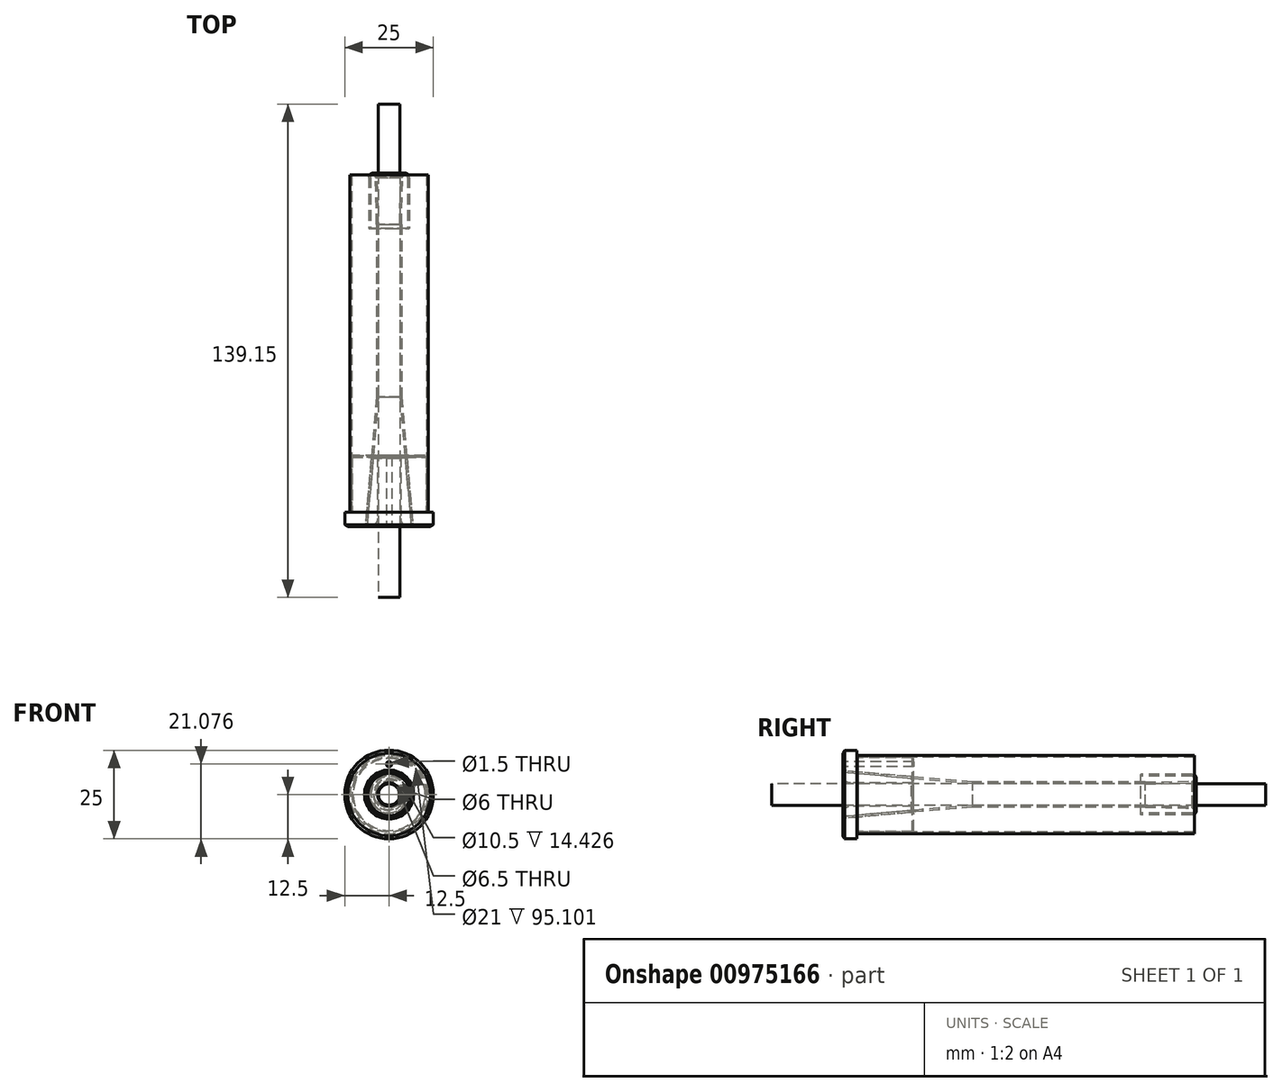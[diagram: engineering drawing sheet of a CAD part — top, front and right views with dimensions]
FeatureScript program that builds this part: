
annotation { "Feature Type Name" : "Feature", "Feature Type Description" : "" }
export const myFeature = defineFeature(function(context is Context, id is Id, definition is map)
    precondition{}
    {
        {
            var Q0;
            Q0=qCreatedBy(makeId("Right.planeOp"),FACE);
            var sketch = newSketch(context, id + "F0", { "sketchPlane" : qUnion([Q0])});
            skLineSegment(sketch, "E0.bottom", {"start": v(-20, 0) * mm, "end": v(119.15, 0) * mm});
            skLineSegment(sketch, "E0.top", {"start": v(-20, 3) * mm, "end": v(119.15, 3) * mm});
            skLineSegment(sketch, "E0.left", {"start": v(-20, 0) * mm, "end": v(-20, 3) * mm});
            skLineSegment(sketch, "E0.right", {"start": v(119.15, 0) * mm, "end": v(119.15, 3) * mm});
            skLineSegment(sketch, "E1", {"start": v(0, 3.25) * mm, "end": v(20, 3.25) * mm});
            skLineSegment(sketch, "E2", {"start": v(0, 3.25) * mm, "end": v(0, 6.2) * mm});
            skLineSegment(sketch, "E3", {"start": v(0, 6.2) * mm, "end": v(20, 4.45) * mm});
            skLineSegment(sketch, "E4", {"start": v(20, 4.45) * mm, "end": v(20, 3.25) * mm});
            skLineSegment(sketch, "E5", {"start": v(0, 6.75) * mm, "end": v(20, 5) * mm});
            skLineSegment(sketch, "E6", {"start": v(0, 6.75) * mm, "end": v(0, 7.83) * mm});
            skLineSegment(sketch, "E7", {"start": v(0, 12.5) * mm, "end": v(4, 12.5) * mm});
            skLineSegment(sketch, "E8", {"start": v(4, 12.5) * mm, "end": v(4, 10.4) * mm});
            skLineSegment(sketch, "E9", {"start": v(4, 10.4) * mm, "end": v(20, 10.4) * mm});
            skLineSegment(sketch, "E10", {"start": v(20, 10.4) * mm, "end": v(20, 9.33) * mm});
            skLineSegment(sketch, "E11", {"start": v(0, 9.33) * mm, "end": v(20, 9.33) * mm, "construction": true});
            skLineSegment(sketch, "E12", {"start": v(20, 8.58) * mm, "end": v(0, 8.58) * mm, "construction": true});
            skLineSegment(sketch, "E13", {"start": v(0, 7.83) * mm, "end": v(20, 7.83) * mm, "construction": true});
            skArc(sketch, "E14", {"start": v(0, 5.5) * mm, "mid": v(0.66, 3.9) * mm, "end": v(2.25, 3.25) * mm});
            skLineSegment(sketch, "E15", {"start": v(0, 5.97) * mm, "end": v(0.21, 6.18) * mm});
            skLineSegment(sketch, "E16", {"start": v(20, 4.26) * mm, "end": v(19.79, 4.47) * mm});
            skLineSegment(sketch, "E17", {"start": v(20, 3.46) * mm, "end": v(19.79, 3.25) * mm});
            skLineSegment(sketch, "E18", {"start": v(0, 11.63) * mm, "end": v(0.5, 12.5) * mm});
            skLineSegment(sketch, "E19", {"start": v(0, 6.95) * mm, "end": v(0.21, 6.73) * mm});
            skLineSegment(sketch, "E20", {"start": v(19.57, 10.4) * mm, "end": v(20, 10.15) * mm});
            skLineSegment(sketch, "E21", {"start": v(20, 5.43) * mm, "end": v(19.35, 5.06) * mm});
            skLineSegment(sketch, "E22", {"start": v(20, 9.33) * mm, "end": v(20, 5) * mm});
            skLineSegment(sketch, "E23", {"start": v(0, 7.83) * mm, "end": v(0, 12.5) * mm});
            skLineSegment(sketch, "E24", {"start": v(80, 10.4) * mm, "end": v(80, 3.8) * mm});
            skLineSegment(sketch, "E25", {"start": v(80, 3.8) * mm, "end": v(98.43, 3.8) * mm});
            skLineSegment(sketch, "E26", {"start": v(80, 10.4) * mm, "end": v(84, 10.4) * mm});
            skLineSegment(sketch, "E27", {"start": v(84, 10.4) * mm, "end": v(84, 5.25) * mm});
            skLineSegment(sketch, "E28", {"start": v(84, 5.25) * mm, "end": v(98.43, 5.25) * mm});
            skLineSegment(sketch, "E29", {"start": v(80, 9.33) * mm, "end": v(84, 9.33) * mm, "construction": true});
            skLineSegment(sketch, "E30", {"start": v(80, 8.58) * mm, "end": v(84, 8.58) * mm, "construction": true});
            skLineSegment(sketch, "E31", {"start": v(80, 7.83) * mm, "end": v(84, 7.83) * mm, "construction": true});
            skLineSegment(sketch, "E32", {"start": v(98.43, 5.25) * mm, "end": v(98.43, 3.8) * mm, "construction": true});
            skArc(sketch, "E33", {"start": v(98.43, 5.25) * mm, "mid": v(99.15, 4.53) * mm, "end": v(98.43, 3.8) * mm});
            skArc(sketch, "E34", {"start": v(84, 7.68) * mm, "mid": v(84.71, 5.96) * mm, "end": v(86.43, 5.25) * mm});
            skLineSegment(sketch, "E35", {"start": v(80.43, 10.4) * mm, "end": v(80, 10.15) * mm});
            skArc(sketch, "E36", {"start": v(80, 6.05) * mm, "mid": v(80.66, 4.46) * mm, "end": v(82.25, 3.8) * mm});
            skLineSegment(sketch, "E37", {"start": v(82, 10.4) * mm, "end": v(82, 9.33) * mm, "construction": true});
            skLineSegment(sketch, "E38.MirrorCS", {"start": v(83.57, 10.4) * mm, "end": v(84, 10.15) * mm});
            skLineSegment(sketch, "E39.bottom", {"start": v(4.05, 11) * mm, "end": v(99.15, 11) * mm});
            skLineSegment(sketch, "E39.top", {"start": v(4.05, 10.5) * mm, "end": v(99.15, 10.5) * mm});
            skLineSegment(sketch, "E39.left", {"start": v(4.05, 11) * mm, "end": v(4.05, 10.5) * mm});
            skLineSegment(sketch, "E39.right", {"start": v(99.15, 11) * mm, "end": v(99.15, 10.5) * mm});
            skPoint(sketch, "E40", {"position": v(99.15, 4.53) * mm});
            skSolve(sketch);
        }
        {
            var Q0;
            Q0=qCreatedBy(makeId("Front.planeOp"),FACE);
            var sketch = newSketch(context, id + "F1", { "sketchPlane" : qUnion([Q0])});
            skPoint(sketch, "E41.0", {"position": v(0, 8.58) * mm});
            skPoint(sketch, "E42.0", {"position": v(0, 9.33) * mm});
            skCircle(sketch, "E43", {"center": v(0, 8.58) * mm, "radius": 0.75 * mm});
            skLineSegment(sketch, "E44", {"start": v(0, 0) * mm, "end": v(2.21, 0) * mm, "construction": true});
            skCircle(sketch, "E45.MirrorC", {"center": v(0, -8.58) * mm, "radius": 0.75 * mm});
            skSolve(sketch);
        }
        {
            var Q0;
            Q0=qCreatedBy(makeId("Right.planeOp"),FACE);
            var sketch = newSketch(context, id + "F2", { "sketchPlane" : qUnion([Q0])});
            skLineSegment(sketch, "E46.0", {"start": v(-20, 0) * mm, "end": v(119.15, 0) * mm, "construction": true});
            skLineSegment(sketch, "E47.0", {"start": v(-20, 3) * mm, "end": v(119.15, 3) * mm});
            skLineSegment(sketch, "E48.0", {"start": v(0, 6.2) * mm, "end": v(20, 4.45) * mm});
            skLineSegment(sketch, "E49.0", {"start": v(84, 5.25) * mm, "end": v(98.43, 5.25) * mm});
            skArc(sketch, "E50.0", {"start": v(98.43, 5.25) * mm, "mid": v(99.15, 4.53) * mm, "end": v(98.43, 3.8) * mm});
            skLineSegment(sketch, "E51.0", {"start": v(80, 3.8) * mm, "end": v(98.43, 3.8) * mm, "construction": true});
            skLineSegment(sketch, "E52", {"start": v(20, 4.45) * mm, "end": v(36.57, 3) * mm});
            skLineSegment(sketch, "E53.0", {"start": v(20.03, 4.95) * mm, "end": v(36.57, 3.5) * mm});
            skLineSegment(sketch, "E53.1", {"start": v(0, 6.7) * mm, "end": v(20.03, 4.95) * mm});
            skLineSegment(sketch, "E54", {"start": v(0, 6.7) * mm, "end": v(0, 6.2) * mm});
            skLineSegment(sketch, "E55", {"start": v(36.57, 3.5) * mm, "end": v(85.22, 3.5) * mm});
            skArc(sketch, "E56.0", {"start": v(98.43, 5.75) * mm, "mid": v(99.65, 4.53) * mm, "end": v(98.43, 3.3) * mm});
            skLineSegment(sketch, "E56.1", {"start": v(84, 5.75) * mm, "end": v(98.43, 5.75) * mm});
            skLineSegment(sketch, "E57", {"start": v(84, 5.75) * mm, "end": v(84, 5.25) * mm});
            skLineSegment(sketch, "E58", {"start": v(85.22, 3.5) * mm, "end": v(98.43, 3.8) * mm});
            skLineSegment(sketch, "E59", {"start": v(98.43, 3.3) * mm, "end": v(85.22, 3) * mm});
            skSolve(sketch);
        }
        {
            var Q0;
            Q0=makeQuery(id+"F0.imprint","IMPRINT",FACE,{"disambiguationData":[TD([[makeQuery(id+"F0.imprint","IMPRINT",EDGE,{"derivedFrom":sQuery(id+"F0.wireOp",EDGE,"E0.bottom")}),1.0]])]});
            var Q1;
            {var subQ7=sQuery(id+"F0.wireOp",EDGE,"E8");Q1=makeQuery(id+"F0.imprint","IMPRINT",FACE,{"disambiguationData":[TD([[makeQuery(id+"F0.imprint","IMPRINT",EDGE,{"derivedFrom":subQ7}),-1.0]])]});}
            var Q2;
            {var subQ5=sQuery(id+"F0.wireOp",EDGE,"E14");Q2=makeQuery(id+"F0.imprint","IMPRINT",FACE,{"disambiguationData":[TD([[makeQuery(id+"F0.imprint","IMPRINT",EDGE,{"derivedFrom":subQ5}),1.0]])]});}
            var Q3;
            {var subQ1=sQuery(id+"F0.wireOp",EDGE,"E33");Q3=makeQuery(id+"F0.imprint","IMPRINT",FACE,{"disambiguationData":[TD([[makeQuery(id+"F0.imprint","IMPRINT",EDGE,{"derivedFrom":subQ1}),-1.0]])]});}
            var Q4;
            Q4=makeQuery(id+"F0.imprint","IMPRINT",FACE,{"disambiguationData":[TD([[makeQuery(id+"F0.imprint","IMPRINT",EDGE,{"derivedFrom":sQuery(id+"F0.wireOp",EDGE,"E39.bottom")}),-1.0]])]});
            var Q5;
            Q5=sQuery(id+"F0.wireOp",EDGE,"E0.bottom");
            revolve(context, id + "F3", {"surfaceOperationType" : NewSurfaceOperationType.NEW, "entities" : qUnion([Q0, Q1, Q2, Q3, Q4]), "axis" : qUnion([Q5]), "revolveType" : RevolveType.FULL});
        }
        {
            var Q0;
            Q0=makeQuery(id+"F1.imprint","IMPRINT",FACE,{"disambiguationData":[TD([[makeQuery(id+"F1.imprint","IMPRINT",EDGE,{"derivedFrom":sQuery(id+"F1.wireOp",EDGE,"E45.MirrorC")}),-1.0]])]});
            var Q1;
            Q1=makeQuery(id+"F1.imprint","IMPRINT",FACE,{"disambiguationData":[TD([[makeQuery(id+"F1.imprint","IMPRINT",EDGE,{"derivedFrom":sQuery(id+"F1.wireOp",EDGE,"E43")}),1.0]])]});
            extrude(context, id + "F4", {"entities" : qUnion([Q0, Q1]), "operationType" : NewBodyOperationType.REMOVE, "endBound" : BoundingType.THROUGH_ALL, "oppositeDirection" : true, "depth" : 25 * mm, "offsetDistance" : 25 * mm});
        }
        {
            var Q0;
            Q0=makeQuery(id+"F2.imprint","IMPRINT",FACE,{"disambiguationData":[TD([[makeQuery(id+"F2.imprint","IMPRINT",EDGE,{"derivedFrom":sQuery(id+"F2.wireOp",EDGE,"E48.0")}),1.0]])]});
            var Q1;
            Q1=sQuery(id+"F2.wireOp",EDGE,"E46.0");
            revolve(context, id + "F5", {"surfaceOperationType" : NewSurfaceOperationType.NEW, "entities" : qUnion([Q0]), "axis" : qUnion([Q1]), "revolveType" : RevolveType.FULL});
        }
    });
